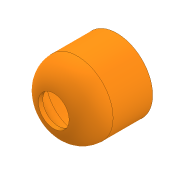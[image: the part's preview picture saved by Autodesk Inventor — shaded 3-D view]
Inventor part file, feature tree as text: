
AUTODESK INVENTOR PART (.ipt)
format: ipt  version: 2020 (Build 240168000, 168)  size: 236,032 bytes
history: native  units: in
note: dims shown in document units (in); Inventor stores cm internally (conversion verified against a paired STEP export)
features: sketch x6, extrude x5, chamfer x1, revolve x1, projected_geometry x1
ambient origin geometry x8: Origin, YZ Plane, XZ Plane, XY Plane, X Axis, Y Axis, Z Axis, Center Point
bodies: Solid1 (feature_tree)
feature tree (14):
  extrude  "Extrusion1"  Depth=0.315in TaperAngle=0.0deg
  chamfer  "Chamfer1"  Distance=0.315in
  extrude  "Extrusion2"  Depth=2.3622in TaperAngle=360.0deg
  extrude  "Extrusion3"  Depth=0.0197in TaperAngle=0.0deg
  extrude  "Extrusion4"  Depth=0.1575in TaperAngle=0.0deg
  extrude  "Extrusion5"  Depth=0.1575in TaperAngle=0.0deg
  revolve  "Revolution1"  [1 undecoded]
  sketch  "Sketch1"  dims[d0=0.4724in d1=0.315in d2=0.0in d3=0.315in d4=0.125in d5=0.0137in]
  sketch  "Sketch2"  dims[d6=0.0157in d7=2.3622in d9=360.0deg]
  sketch  "Sketch3"  dims[d11=0.315in d12=0.0in d13=0.0197in d14=0.0in]
  projected_geometry  "Projected Loop1"
  sketch  "Sketch4"  dims[d15=2.5591in d16=0.1575in d17=0.0in]
  sketch  "Sketch5"  dims[d18=0.1575in d19=1.2598in d20=0.0in]
  sketch  "Sketch6"  dims[d21=1.1024in d22=0.5512in d23=0.8465in d24=0.1575in d25=90.0deg]
note: 1 required parameter value undecoded (feature->parameter linkage not recoverable at this tier; creation-order binding heuristic only, values carry confidence <= 0.55)
